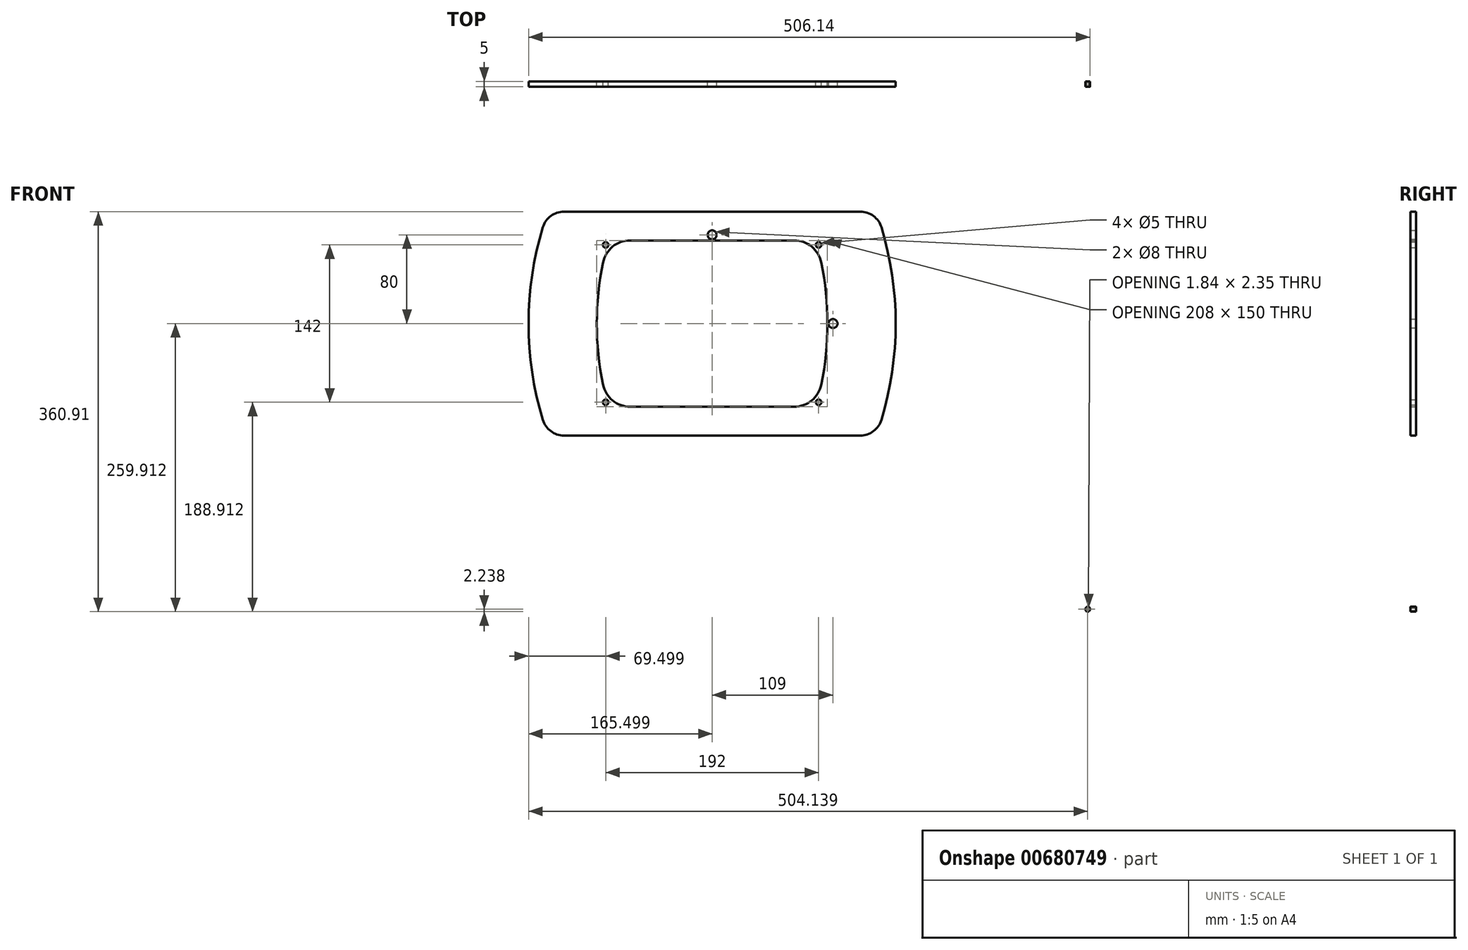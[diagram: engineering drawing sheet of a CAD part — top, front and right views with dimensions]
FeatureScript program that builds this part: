
annotation { "Feature Type Name" : "Feature", "Feature Type Description" : "" }
export const myFeature = defineFeature(function(context is Context, id is Id, definition is map)
    precondition{}
    {
        {
            var Q0;
            Q0=qCreatedBy(makeId("Front.planeOp"),FACE);
            var sketch = newSketch(context, id + "F0", { "sketchPlane" : qUnion([Q0])});
            skFitSpline(sketch, "E0", {"points": [v(706.62, 27.8) * mm, v(706.65, 27.8) * mm, v(706.71, 27.8) * mm, v(706.82, 27.8) * mm, v(707.08, 27.76) * mm, v(707.3, 27.69) * mm, v(707.52, 27.62) * mm, v(707.88, 27.38) * mm, v(708.07, 27.17) * mm, v(708.23, 27) * mm, v(708.36, 26.76) * mm, v(708.5, 26.42) * mm, v(708.6, 26.12) * mm, v(708.63, 25.77) * mm, v(708.65, 25.46) * mm, v(708.6, 25.09) * mm, v(708.56, 24.86) * mm, v(708.36, 24.37) * mm, v(708.23, 24.2) * mm, v(708.05, 23.94) * mm, v(707.84, 23.77) * mm, v(707.61, 23.62) * mm, v(707.37, 23.5) * mm, v(707.09, 23.41) * mm, v(706.82, 23.38) * mm, v(706.47, 23.34) * mm, v(706, 23.49) * mm, v(705.8, 23.57) * mm, v(705.54, 23.73) * mm, v(705.32, 23.92) * mm, v(705.15, 24.07) * mm, v(704.9, 24.49) * mm, v(704.82, 24.73) * mm, v(704.71, 25.11) * mm, v(704.65, 25.38) * mm, v(704.7, 25.99) * mm, v(704.76, 26.27) * mm, v(704.86, 26.62) * mm, v(705, 26.9) * mm, v(705.18, 27.14) * mm, v(705.43, 27.37) * mm, v(705.58, 27.5) * mm, v(706.03, 27.72) * mm, v(706.16, 27.74) * mm, v(706.42, 27.8) * mm, v(706.53, 27.8) * mm, v(706.59, 27.8) * mm, v(706.62, 27.8) * mm]});
            skFitSpline(sketch, "E1", {"points": [v(706.63, 26.75) * mm, v(706.65, 26.75) * mm, v(706.7, 26.75) * mm, v(706.76, 26.75) * mm, v(706.88, 26.73) * mm, v(706.94, 26.7) * mm, v(707.03, 26.67) * mm, v(707.1, 26.64) * mm, v(707.18, 26.57) * mm, v(707.24, 26.52) * mm, v(707.38, 26.35) * mm, v(707.47, 26.15) * mm, v(707.52, 26) * mm, v(707.56, 25.81) * mm, v(707.57, 25.63) * mm, v(707.57, 25.44) * mm, v(707.53, 25.24) * mm, v(707.5, 25.09) * mm, v(707.4, 24.86) * mm, v(707.34, 24.78) * mm, v(707.25, 24.67) * mm, v(707.16, 24.59) * mm, v(707.05, 24.52) * mm, v(706.95, 24.46) * mm, v(706.8, 24.42) * mm, v(706.74, 24.42) * mm, v(706.5, 24.4) * mm, v(706.42, 24.45) * mm, v(706.3, 24.49) * mm, v(706.19, 24.56) * mm, v(706.1, 24.63) * mm, v(706, 24.74) * mm, v(705.95, 24.8) * mm, v(705.85, 25) * mm, v(705.84, 25.03) * mm, v(705.77, 25.24) * mm, v(705.75, 25.44) * mm, v(705.73, 25.49) * mm, v(705.73, 25.73) * mm, v(705.77, 25.95) * mm, v(705.8, 26.05) * mm, v(705.85, 26.18) * mm, v(705.9, 26.29) * mm, v(705.97, 26.4) * mm, v(706.02, 26.47) * mm, v(706.15, 26.6) * mm, v(706.22, 26.64) * mm, v(706.32, 26.7) * mm, v(706.42, 26.72) * mm, v(706.5, 26.75) * mm, v(706.56, 26.75) * mm, v(706.6, 26.75) * mm, v(706.63, 26.75) * mm]});
            skArc(sketch, "E2", {"start": v(215.34, 196.47) * mm, "mid": v(222.56, 186.2) * mm, "end": v(234.48, 182.25) * mm});
            skArc(sketch, "E3", {"start": v(501.54, 182.25) * mm, "mid": v(513.46, 186.2) * mm, "end": v(520.68, 196.47) * mm});
            skArc(sketch, "E4", {"start": v(520.68, 370.04) * mm, "mid": v(513.46, 380.31) * mm, "end": v(501.54, 384.25) * mm});
            skArc(sketch, "E5", {"start": v(234.48, 384.25) * mm, "mid": v(222.56, 380.31) * mm, "end": v(215.34, 370.04) * mm});
            skArc(sketch, "E6", {"start": v(215.34, 370.04) * mm, "mid": v(202.5, 283.25) * mm, "end": v(215.34, 196.47) * mm});
            skLineSegment(sketch, "E7", {"start": v(234.48, 182.25) * mm, "end": v(501.54, 182.25) * mm});
            skArc(sketch, "E8", {"start": v(520.68, 196.47) * mm, "mid": v(533.5, 283.25) * mm, "end": v(520.68, 370.04) * mm});
            skLineSegment(sketch, "E9", {"start": v(501.54, 384.25) * mm, "end": v(234.48, 384.25) * mm});
            skCircle(sketch, "E10", {"center": v(464, 354.25) * mm, "radius": 2.5 * mm});
            skCircle(sketch, "E11", {"center": v(272, 354.25) * mm, "radius": 2.5 * mm});
            skCircle(sketch, "E12", {"center": v(272, 212.25) * mm, "radius": 2.5 * mm});
            skCircle(sketch, "E13", {"center": v(464, 212.25) * mm, "radius": 2.5 * mm});
            skCircle(sketch, "E14", {"center": v(368, 363.25) * mm, "radius": 4 * mm});
            skCircle(sketch, "E15", {"center": v(477, 283.25) * mm, "radius": 4 * mm});
            skLineSegment(sketch, "E16", {"start": v(441.96, 208.25) * mm, "end": v(294.06, 208.25) * mm});
            skArc(sketch, "E17", {"start": v(269.57, 338.25) * mm, "mid": v(264, 283.25) * mm, "end": v(269.57, 228.25) * mm});
            skLineSegment(sketch, "E18", {"start": v(294.06, 358.25) * mm, "end": v(441.96, 358.25) * mm});
            skArc(sketch, "E19", {"start": v(466.45, 228.25) * mm, "mid": v(472, 283.25) * mm, "end": v(466.45, 338.25) * mm});
            skArc(sketch, "E20", {"start": v(269.57, 228.25) * mm, "mid": v(278.25, 213.89) * mm, "end": v(294.06, 208.25) * mm});
            skArc(sketch, "E21", {"start": v(294.06, 358.25) * mm, "mid": v(278.25, 352.62) * mm, "end": v(269.57, 338.25) * mm});
            skArc(sketch, "E22", {"start": v(466.45, 338.25) * mm, "mid": v(457.77, 352.62) * mm, "end": v(441.96, 358.25) * mm});
            skArc(sketch, "E23", {"start": v(441.96, 208.25) * mm, "mid": v(457.77, 213.89) * mm, "end": v(466.45, 228.25) * mm});
            skLineSegment(sketch, "E24", {"start": v(533.5, 381.97) * mm, "end": v(533.5, 171.81) * mm});
            skPoint(sketch, "E25.startSnap0", {"position": v(202.5, 283.25) * mm});
            skSolve(sketch);
        }
        {
            var Q0;
            Q0 = qSketchRegion(id + "F0", true);
            extrude(context, id + "F1", {"entities" : qUnion([Q0]), "depth" : 5 * mm, "offsetDistance" : 25.4 * mm});
        }
    });
